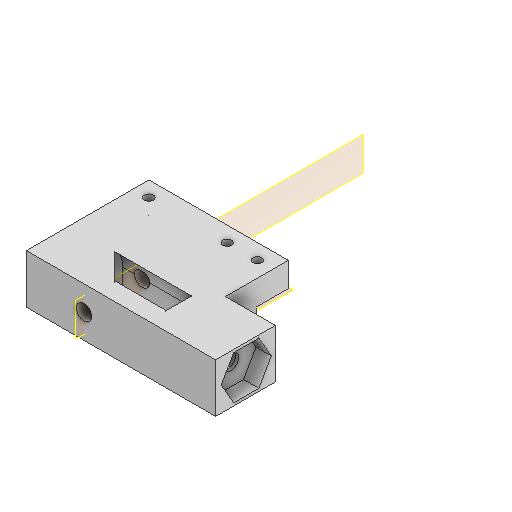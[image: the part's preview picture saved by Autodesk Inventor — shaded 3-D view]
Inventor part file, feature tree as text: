
AUTODESK INVENTOR PART (.ipt)
format: ipt  version: 2022 (Build 260153000, 153)  size: 298,496 bytes
history: native  units: mm
features: reference x16, extrude x11, sketch x11, plane x7, projected_geometry x5, other x5
ambient origin geometry x8: Origin, YZ Plane, XZ Plane, XY Plane, X Axis, Y Axis, Z Axis, Center Point
bodies: Body1 (feature_tree)
feature tree (55):
  plane  "Arbeitsebene6"
  extrude  "Extrusion12"  Depth=0.5mm
  extrude  "Extrusion13"  Depth=12.5mm TaperAngle=0.0deg
  plane  "Arbeitsebene7"
  extrude  "Extrusion15"  Depth=5.0mm TaperAngle=0.0deg
  sketch  "Skizze19"  dims[d71=12.3mm d72=10.0mm d73=0.0mm]
  plane  "Arbeitsebene8"
  extrude  "Extrusion16"  Depth=10.0mm TaperAngle=0.0deg
  sketch  "Skizze20"  dims[d74=17.0mm d75=18.0mm]
  plane  "Arbeitsebene9"
  extrude  "Extrusion17"  Depth=18.0mm
  plane  "Arbeitsebene10"
  sketch  "Skizze21"  dims[d76=35.97mm d77=0.0mm d78=21.0mm]
  plane  "Arbeitsebene11"
  extrude  "Extrusion18"  Depth=21.0mm
  extrude  "Extrusion19"  Depth=1.2mm
  extrude  "Extrusion20"  Depth=14.0mm TaperAngle=0.0deg
  extrude  "Extrusion21"  Depth=0.5mm
  plane  "Arbeitsebene12"
  extrude  "Extrusion22"  TaperAngle=0.0deg  [1 undecoded]
  extrude  "Extrusion23"  Depth=0.872665mm
  sketch  "Skizze13"  dims[d58=8.0mm d59=0.0mm d60=0.5mm]
  reference  "Referenz11"
  reference  "Referenz12"
  reference  "Referenz13"
  reference  "Referenz14"
  sketch  "Skizze16"  dims[d62=8.0mm d63=0.0mm d66=12.5mm d67=0.0mm]
  projected_geometry  "Projizierte Kontur9"
  reference  "Referenz15"
  sketch  "Skizze18"  dims[d68=0.1mm d69=5.0mm d70=0.0mm]
  reference  "Referenz17"
  reference  "Referenz18"
  reference  "Referenz19"
  reference  "Referenz20"
  reference  "Referenz21"
  reference  "Referenz22"
  reference  "Referenz23"
  reference  "Referenz24"
  reference  "Referenz25"
  sketch  "Skizze22"  dims[d79=45.0deg d80=1.2mm]
  projected_geometry  "Projizierte Kontur10"
  sketch  "Skizze23"  dims[d81=14.0mm d82=0.0mm d83=14.0mm d84=0.0mm]
  projected_geometry  "Projizierte Kontur11"
  sketch  "Skizze24"  dims[d85=1.0mm d86=0.0mm d87=0.5mm]
  projected_geometry  "Projizierte Kontur12"
  sketch  "Skizze25"  dims[d88=10.0mm d89=0.0mm d90=0.0mm d91=0.0mm]
  reference  "Referenz26"
  reference  "Referenz27"
  sketch  "Skizze26"  dims[d15=0.5mm d16=0.872665mm d17=0.5mm d18=0.872665mm]
  projected_geometry  "Projizierte Kontur13"
  other  "Assemlby_lightsheet_generator_passive_v2.iam"
  other  "30_Scanlens_Laseradaper_lid_v1:1"
  other  "00_Thorlabs_LJ1878L1-A-Step:1"
  other  "00_CCTV_lens_M12_25mm_5mp:1"
  other  "00_SMAConnector_fiber copy:1"
note: 1 required parameter value undecoded (feature->parameter linkage not recoverable at this tier; creation-order binding heuristic only, values carry confidence <= 0.55)
